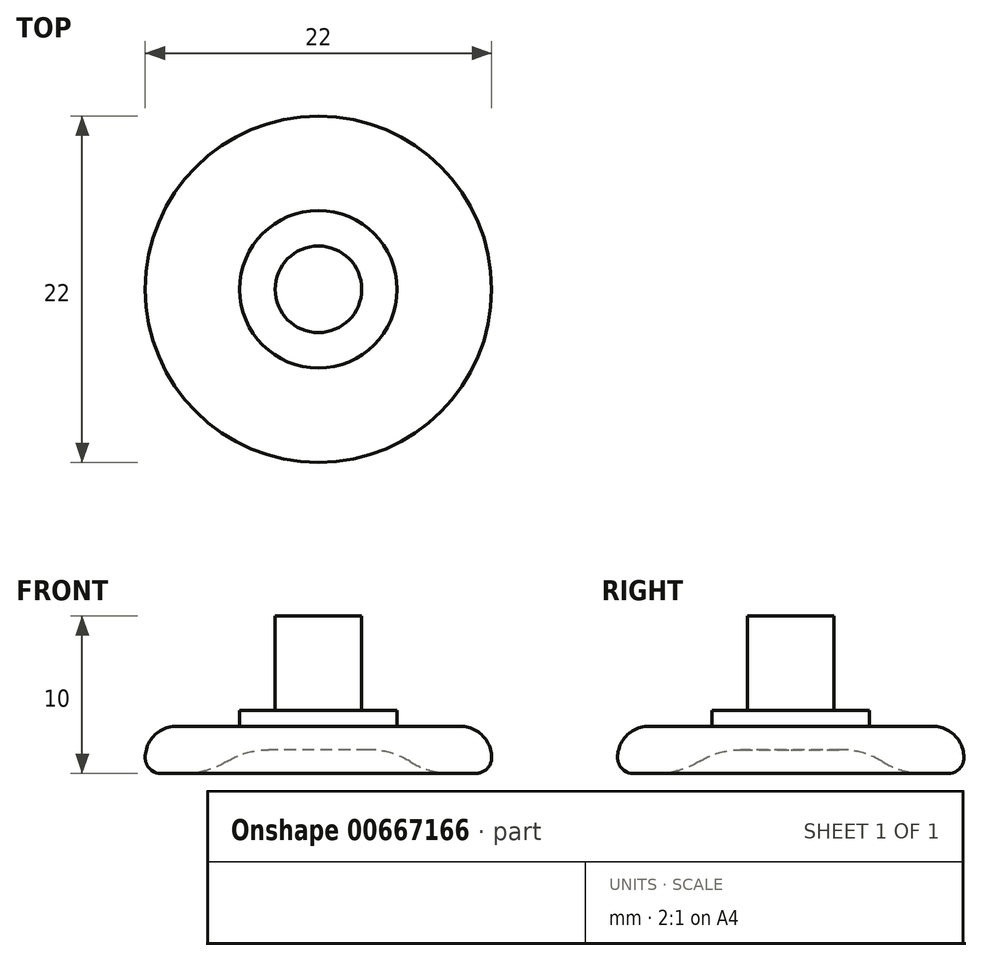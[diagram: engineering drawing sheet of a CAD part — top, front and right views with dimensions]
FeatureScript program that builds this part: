
annotation { "Feature Type Name" : "Feature", "Feature Type Description" : "" }
export const myFeature = defineFeature(function(context is Context, id is Id, definition is map)
    precondition{}
    {
        {
            assignVariable(context, id + "F0", {"name" : "PlateThickness", "anyValue" : 3});
        }
        {
            var Q0;
            Q0=qCreatedBy(makeId("Top.planeOp"),FACE);
            var sketch = newSketch(context, id + "F1", { "sketchPlane" : qUnion([Q0])});
            skCircle(sketch, "E0", {"center": v(0, 0) * mm, "radius": 11 * mm});
            skCircle(sketch, "E1", {"center": v(0, 0) * mm, "radius": 2.75 * mm});
            skCircle(sketch, "E2", {"center": v(0, 0) * mm, "radius": 5 * mm});
            skSolve(sketch);
        }
        {
            var Q0;
            Q0=makeQuery(id+"F1.imprint","IMPRINT",FACE,{"disambiguationData":[TD([[makeQuery(id+"F1.imprint","IMPRINT",EDGE,{"derivedFrom":sQuery(id+"F1.wireOp",EDGE,"E0")}),1.0]])]});
            var Q1;
            Q1=makeQuery(id+"F1.imprint","IMPRINT",FACE,{"disambiguationData":[TD([[makeQuery(id+"F1.imprint","IMPRINT",EDGE,{"derivedFrom":sQuery(id+"F1.wireOp",EDGE,"eSHOdHc0-WQbQ-iaRl-N4qy-GDKkVdP7ETnB")}),-1.0]])]});
            var Q2;
            Q2=makeQuery(id+"F1.imprint","IMPRINT",FACE,{"disambiguationData":[TD([[makeQuery(id+"F1.imprint","IMPRINT",EDGE,{"derivedFrom":sQuery(id+"F1.wireOp",EDGE,"E1")}),-1.0]])]});
            extrude(context, id + "F2", {"entities" : qUnion([Q0, Q1, Q2]), "depth" : (getVariable(context, 'PlateThickness')) * mm, "offsetDistance" : 25 * mm});
        }
        {
            var Q0;
            Q0=makeQuery(id+"F1.imprint","IMPRINT",FACE,{"disambiguationData":[TD([[makeQuery(id+"F1.imprint","IMPRINT",EDGE,{"derivedFrom":sQuery(id+"F1.wireOp",EDGE,"E1")}),1.0]])]});
            extrude(context, id + "F3", {"entities" : qUnion([Q0]), "operationType" : NewBodyOperationType.ADD, "depth" : (getVariable(context, 'PlateThickness') + 7) * mm, "offsetDistance" : 25 * mm, "hasSecondDirection" : true, "secondDirectionOppositeDirection" : false, "secondDirectionDepth" : 1.5 * mm});
        }
        {
            var Q0;
            Q0=makeQuery(id+"F1.imprint","IMPRINT",FACE,{"disambiguationData":[TD([[makeQuery(id+"F1.imprint","IMPRINT",EDGE,{"derivedFrom":sQuery(id+"F1.wireOp",EDGE,"E1")}),-1.0]])]});
            var Q1;
            Q1=makeQuery(id+"F2.opExtrude","CAP_FACE",FACE,{"disambiguationData":[OSD([sQuery(id+"F1.wireOp",EDGE,"E0"),sQuery(id+"F1.wireOp",EDGE,"eSHOdHc0-WQbQ-iaRl-N4qy-GDKkVdP7ETnB")])],"isStart":false});
            extrude(context, id + "F4", {"entities" : qUnion([Q0]), "operationType" : NewBodyOperationType.ADD, "depth" : (getVariable(context, 'PlateThickness') + 1) * mm, "offsetDistance" : 25 * mm, "hasSecondDirection" : true, "secondDirectionBound" : SecondDirectionBoundingType.UP_TO_SURFACE, "secondDirectionOppositeDirection" : false, "secondDirectionDepth" : 25 * mm, "secondDirectionBoundEntityFace" : qUnion([Q1])});
        }
        {
            var Q0;
            Q0=makeQuery(id+"F2.opExtrude","CAP_EDGE",EDGE,{"disambiguationData":[OSD([sQuery(id+"F1.wireOp",EDGE,"E0")])],"isStart":true});
            fillet(context, id + "F5", {"entities" : qUnion([Q0]), "radius" : 1 * mm, "tangentPropagation" : true, "allowEdgeOverflow" : false});
        }
        {
            var Q0;
            Q0=makeQuery(id+"F2.opExtrude","CAP_EDGE",EDGE,{"disambiguationData":[OSD([sQuery(id+"F1.wireOp",EDGE,"E1")])],"isStart":true});
            chamfer(context, id + "F6", {"entities" : qUnion([Q0]), "width" : 4 * mm, "tangentPropagation" : true});
        }
        {
            var Q0;
            {var subQ0=sQuery(id+"F1.wireOp",EDGE,"E1");Q0=makeQuery(id+"F6.opChamfer","BLEND_EDGE",EDGE,{"blendedFrom":[makeQuery(id+"F2.opExtrude","CAP_EDGE",EDGE,{"disambiguationData":[OSD([subQ0])],"isStart":true}),makeQuery(id+"F3.opExtrude","CAP_FACE",FACE,{"disambiguationData":[OSD([subQ0])],"isStart":true})],"blendedInto":[makeQuery(id+"F3.opExtrude","CAP_FACE",FACE,{"disambiguationData":[OSD([subQ0])],"isStart":true})]});}
            fillet(context, id + "F7", {"entities" : qUnion([Q0]), "radius" : 5 * mm, "tangentPropagation" : true, "allowEdgeOverflow" : false});
        }
        {
            var Q0;
            {var subQ0=sQuery(id+"F1.wireOp",EDGE,"E1");Q0=makeQuery(id+"F6.opChamfer","BLEND_EDGE",EDGE,{"blendedFrom":[makeQuery(id+"F2.opExtrude","CAP_EDGE",EDGE,{"disambiguationData":[OSD([subQ0])],"isStart":true}),makeQuery(id+"F2.opExtrude","CAP_FACE",FACE,{"disambiguationData":[OSD([sQuery(id+"F1.wireOp",EDGE,"E0"),subQ0])],"isStart":true})],"blendedInto":[makeQuery(id+"F2.opExtrude","CAP_FACE",FACE,{"disambiguationData":[OSD([sQuery(id+"F1.wireOp",EDGE,"E0"),subQ0])],"isStart":true})]});}
            fillet(context, id + "F8", {"entities" : qUnion([Q0]), "radius" : 5 * mm, "tangentPropagation" : true, "allowEdgeOverflow" : false});
        }
        {
            var Q0;
            Q0=makeQuery(id+"F2.opExtrude","CAP_EDGE",EDGE,{"disambiguationData":[OSD([sQuery(id+"F1.wireOp",EDGE,"E0")])],"isStart":false});
            fillet(context, id + "F9", {"entities" : qUnion([Q0]), "radius" : 2 * mm, "tangentPropagation" : true, "allowEdgeOverflow" : false});
        }
    });
